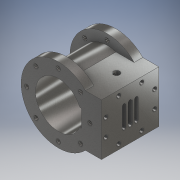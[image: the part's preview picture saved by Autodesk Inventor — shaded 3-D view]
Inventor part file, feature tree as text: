
AUTODESK INVENTOR PART (.ipt)
format: ipt  version: 2017 (Build 210142000, 142)  size: 307,712 bytes
history: native  units: mm
features: extrude x4, sketch x4, plane x2, mirror x1, projected_geometry x1
ambient origin geometry x8: Origin, YZ Plane, XZ Plane, XY Plane, X Axis, Y Axis, Z Axis, Center Point
bodies: Solid1 (feature_tree)
feature tree (12):
  extrude  "Extrusion1"  Depth=40.0mm TaperAngle=0.0deg
  plane  "Work Plane1"
  sketch  "Sketch6"  dims[d21=3.0mm d22=3.0mm d23=1.5mm d24=2.5mm d25=2.5mm d26=2.5mm d29=11.0mm d30=0.0mm]
  extrude  "Extrusion5"  Depth=3.0mm
  extrude  "Extrusion6"  Depth=1.5mm TaperAngle=0.0deg
  plane  "Work Plane2"
  mirror  "Mirror1"
  extrude  "Extrusion8"  Depth=10.0mm TaperAngle=0.0deg
  sketch  "Sketch2"  dims[d1=80.0mm d2=52.0mm d3=32.0mm d4=6.0mm d5=6.0mm d6=3.0mm d7=30.0mm d8=18.0mm d9=36.0mm d10=360.0deg d11=40.0mm d12=0.0mm]
  sketch  "Sketch4"  dims[d13=0.0mm d18=3.0mm]
  sketch  "Sketch9"  dims[d31=38.0mm d32=52.0mm d33=34.0mm d34=0.0mm d35=20.0mm d36=22.0mm d37=0.0mm d38=18.0mm d39=0.0mm d40=16.0mm d41=38.0mm d42=12.25mm d43=19.0mm d44=37.0mm d45=38.0mm d46=25.5mm d47=20.0mm d48=17.0mm d49=40.0mm d50=19.0mm d51=0.0mm d52=37.0mm d53=3.0mm d54=1.0mm d55=1.0mm d56=3.0mm d57=4.5mm d58=28.0mm d59=12.25mm d60=13.0mm d61=37.0mm d62=17.5mm d63=17.5mm d64=19.0mm d65=0.0mm d66=25.75mm d67=25.75mm d68=37.0mm d69=40.0mm d70=37.0mm d71=37.0mm d72=3.0mm d73=26.0mm d74=36.0mm d75=18.0mm d76=18.0mm d77=0.0mm d81=4.5mm d82=10.0mm d83=0.0mm]
  projected_geometry  "Projected Loop2"
